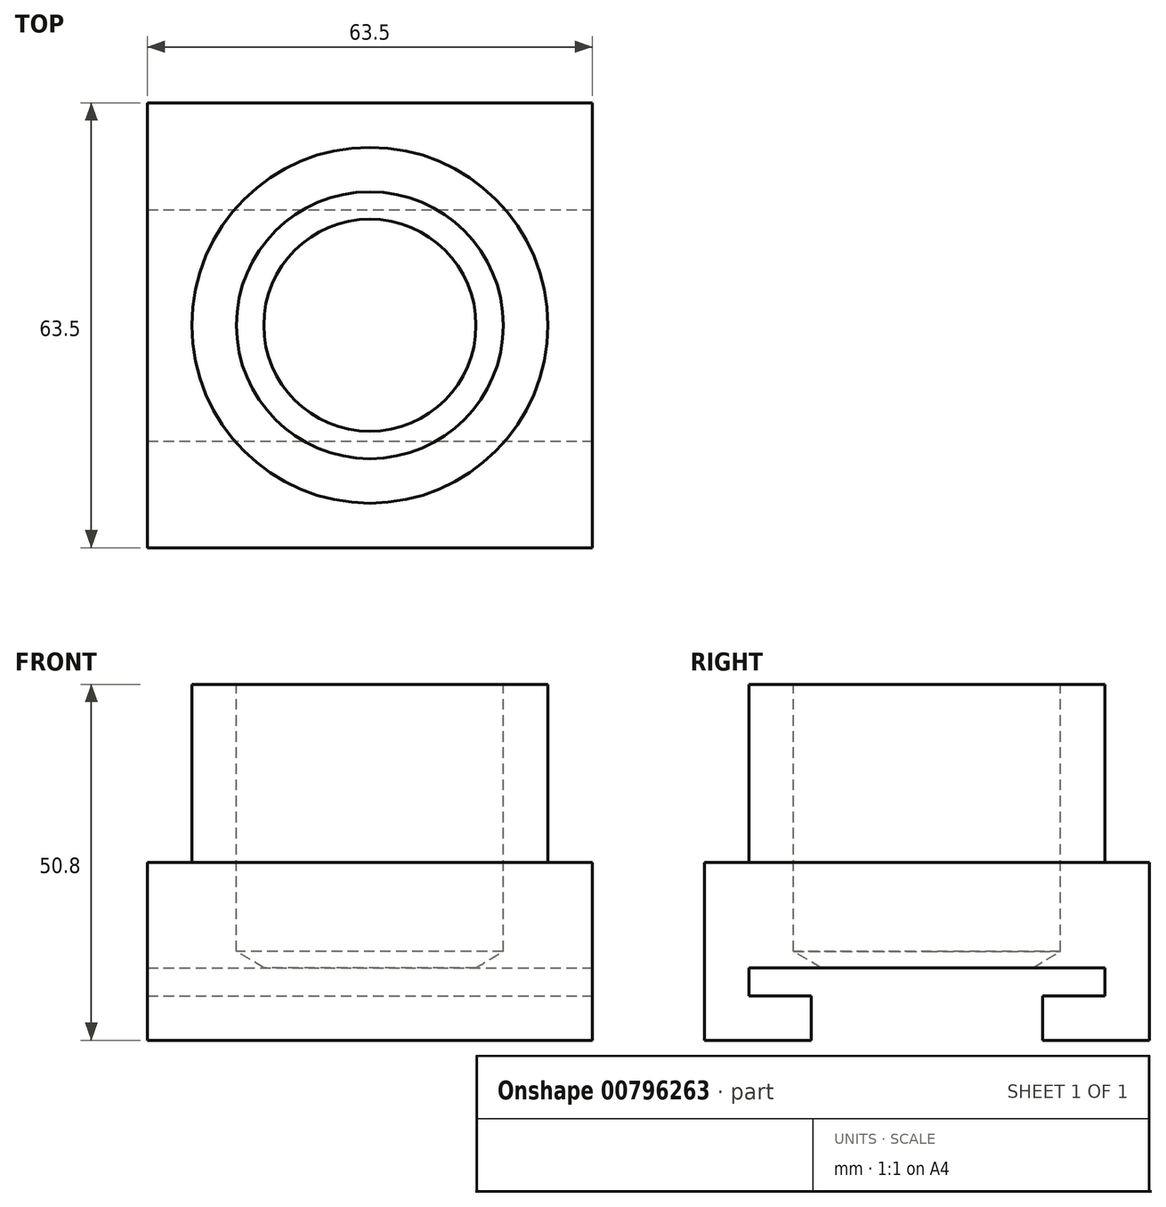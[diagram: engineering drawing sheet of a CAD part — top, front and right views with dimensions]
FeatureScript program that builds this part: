
annotation { "Feature Type Name" : "Feature", "Feature Type Description" : "" }
export const myFeature = defineFeature(function(context is Context, id is Id, definition is map)
    precondition{}
    {
        {
            var Q0;
            Q0=qCreatedBy(makeId("Top.planeOp"),FACE);
            var sketch = newSketch(context, id + "F0", { "sketchPlane" : qUnion([Q0])});
            skCircle(sketch, "E0", {"center": v(0, 0) * mm, "radius": 25.4 * mm});
            skSolve(sketch);
        }
        {
            var Q0;
            Q0 = qSketchRegion(id + "F0", true);
            extrude(context, id + "F1", {"entities" : qUnion([Q0]), "depth" : 25.4 * mm, "offsetDistance" : 25.4 * mm});
        }
        {
            var Q0;
            Q0=makeQuery(id+"F0.imprint","IMPRINT",FACE,{"disambiguationData":[TD([[makeQuery(id+"F0.imprint","IMPRINT",EDGE,{"derivedFrom":sQuery(id+"F0.wireOp",EDGE,"E0")}),1.0]])]});
            var sketch = newSketch(context, id + "F2", { "sketchPlane" : qUnion([Q0])});
            skLineSegment(sketch, "E1.bottom", {"start": v(31.75, 31.75) * mm, "end": v(-31.75, 31.75) * mm});
            skLineSegment(sketch, "E1.top", {"start": v(31.75, -31.75) * mm, "end": v(-31.75, -31.75) * mm});
            skLineSegment(sketch, "E1.left", {"start": v(31.75, 31.75) * mm, "end": v(31.75, -31.75) * mm});
            skLineSegment(sketch, "E1.right", {"start": v(-31.75, 31.75) * mm, "end": v(-31.75, -31.75) * mm});
            skPoint(sketch, "E1.middle", {"position": v(0, 0) * mm});
            skSolve(sketch);
        }
        {
            var Q0;
            Q0 = qSketchRegion(id + "F2", true);
            extrude(context, id + "F3", {"entities" : qUnion([Q0]), "operationType" : NewBodyOperationType.ADD, "oppositeDirection" : true, "depth" : 25.4 * mm, "offsetDistance" : 25.4 * mm});
        }
        {
            var Q0;
            Q0=makeQuery(id+"F3.opExtrude","SWEPT_FACE",FACE,{"disambiguationData":[OSD([sQuery(id+"F2.wireOp",EDGE,"E1.left")])]});
            var sketch = newSketch(context, id + "F4", { "sketchPlane" : qUnion([Q0])});
            skLineSegment(sketch, "E2", {"start": v(-16.5, -19.05) * mm, "end": v(-16.5, -25.4) * mm});
            skLineSegment(sketch, "E3", {"start": v(-16.5, -25.4) * mm, "end": v(0, -25.4) * mm});
            skLineSegment(sketch, "E4", {"start": v(-25.4, -15.05) * mm, "end": v(0, -15.05) * mm});
            skLineSegment(sketch, "E5", {"start": v(0, -15.05) * mm, "end": v(0, -25.4) * mm, "construction": true});
            skLineSegment(sketch, "E6", {"start": v(-25.4, -15.05) * mm, "end": v(-25.4, -19.05) * mm});
            skLineSegment(sketch, "E7", {"start": v(-25.4, -19.05) * mm, "end": v(-16.5, -19.05) * mm});
            skLineSegment(sketch, "E8.MirrorCS", {"start": v(25.4, -15.05) * mm, "end": v(0, -15.05) * mm});
            skLineSegment(sketch, "E9.MirrorCS", {"start": v(25.4, -15.05) * mm, "end": v(25.4, -19.05) * mm});
            skLineSegment(sketch, "E10.MirrorCS", {"start": v(25.4, -19.05) * mm, "end": v(16.5, -19.05) * mm});
            skLineSegment(sketch, "E11.MirrorCS", {"start": v(16.51, -19.05) * mm, "end": v(16.51, -25.4) * mm});
            skLineSegment(sketch, "E12.MirrorCS", {"start": v(16.51, -25.4) * mm, "end": v(0, -25.4) * mm});
            skSolve(sketch);
        }
        {
            var Q0;
            Q0 = qSketchRegion(id + "F4", true);
            extrude(context, id + "F5", {"entities" : qUnion([Q0]), "operationType" : NewBodyOperationType.REMOVE, "endBound" : BoundingType.THROUGH_ALL, "oppositeDirection" : true, "depth" : 25.4 * mm, "offsetDistance" : 25.4 * mm});
        }
        {
            var Q0;
            Q0=makeQuery(id+"F1.opExtrude","CAP_FACE",FACE,{"disambiguationData":[OSD([sQuery(id+"F0.wireOp",EDGE,"E0")])],"isStart":false});
            var sketch = newSketch(context, id + "F6", { "sketchPlane" : qUnion([Q0])});
            skPoint(sketch, "E13", {"position": v(0, 0) * mm});
            skSolve(sketch);
        }
        {
            var Q0;
            Q0=sQuery(id+"F6.wireOp",VERTEX,"E13");
            var Q1;
            Q1=makeQuery(id+"F1.opExtrude","SWEPT_BODY",BODY,{"disambiguationData":[OSD([sQuery(id+"F0.wireOp",EDGE,"E0")])]});
            hole(context, id + "F7", {"style" : HoleStyle.SIMPLE, "endStyle" : HoleEndStyle.BLIND, "holeDiameter" : 38.1 * mm, "majorDiameter" : 38.1 * mm, "holeDepth" : 38.1 * mm, "isTappedThrough" : true, "tappedDepth" : 25.4 * mm, "tapClearance" : 3, "startFromSketch" : true, "locations" : qUnion([Q0]), "scope" : qUnion([Q1])});
        }
    });
